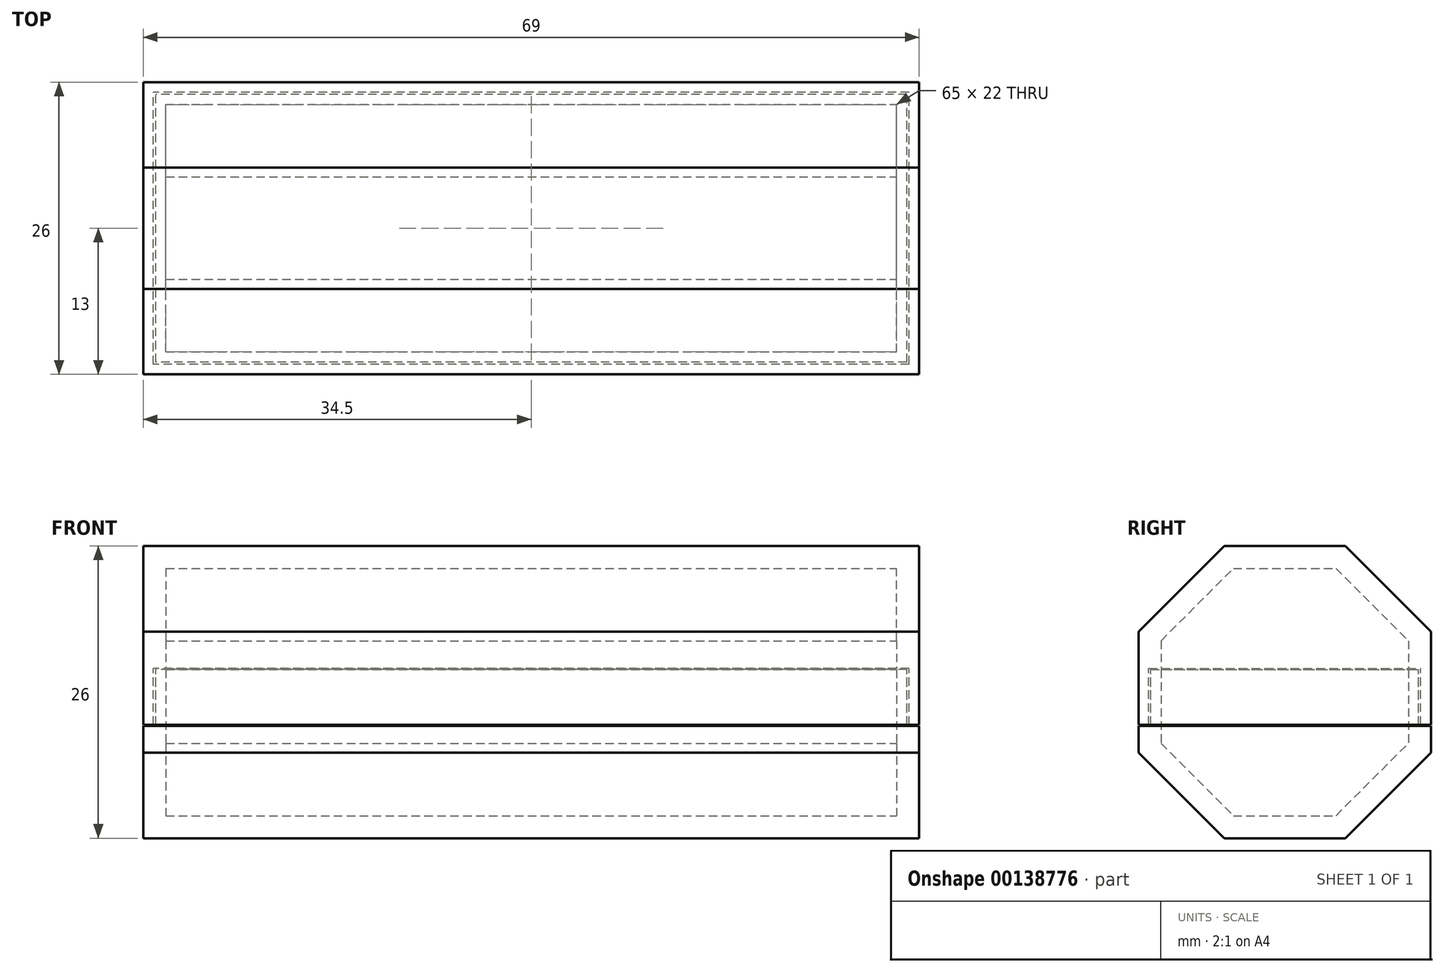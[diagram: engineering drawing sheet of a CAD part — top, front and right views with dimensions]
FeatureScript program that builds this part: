
annotation { "Feature Type Name" : "Feature", "Feature Type Description" : "" }
export const myFeature = defineFeature(function(context is Context, id is Id, definition is map)
    precondition{}
    {
        {
            var Q0;
            Q0=qCreatedBy(makeId("Top.planeOp"),FACE);
            var sketch = newSketch(context, id + "F0", { "sketchPlane" : qUnion([Q0])});
            skLineSegment(sketch, "E0.bottom", {"start": v(34.5, -13) * mm, "end": v(-34.5, -13) * mm});
            skLineSegment(sketch, "E0.top", {"start": v(34.5, 13) * mm, "end": v(-34.5, 13) * mm});
            skLineSegment(sketch, "E0.left", {"start": v(34.5, -13) * mm, "end": v(34.5, 13) * mm});
            skLineSegment(sketch, "E0.right", {"start": v(-34.5, -13) * mm, "end": v(-34.5, 13) * mm});
            skPoint(sketch, "E0.middle", {"position": v(0, 0) * mm});
            skSolve(sketch);
        }
        {
            var Q0;
            Q0 = qSketchRegion(id + "F0", true);
            extrude(context, id + "F1", {"entities" : qUnion([Q0]), "depth" : 15 * mm});
        }
        {
            var Q0;
            Q0=makeQuery(id+"F1.opExtrude","SWEPT_FACE",FACE,{"disambiguationData":[OSD([sQuery(id+"F0.wireOp",EDGE,"E0.left")])]});
            cPlane(context, id + "F2", {"entities" : qUnion([Q0]), "cplaneType" : CPlaneType.OFFSET, "offset" : 2 * mm, "oppositeDirection" : true, "width" : 150 * mm, "height" : 150 * mm});
        }
        {
            var Q0;
            Q0=qCreatedBy(id+"F2.planeOp",FACE);
            var sketch = newSketch(context, id + "F3", { "sketchPlane" : qUnion([Q0])});
            skLineSegment(sketch, "E1.0", {"start": v(13, 15) * mm, "end": v(13, 0) * mm, "construction": true});
            skLineSegment(sketch, "E2.0", {"start": v(-13, 0) * mm, "end": v(13, 0) * mm, "construction": true});
            skLineSegment(sketch, "E3.0", {"start": v(-13, 15) * mm, "end": v(-13, 0) * mm, "construction": true});
            skLineSegment(sketch, "E4.0", {"start": v(-13, 15) * mm, "end": v(13, 15) * mm, "construction": true});
            skLineSegment(sketch, "E5.1", {"start": v(-11, 15) * mm, "end": v(-11, 2) * mm, "construction": true});
            skLineSegment(sketch, "E5.2", {"start": v(-11, 2) * mm, "end": v(11, 2) * mm, "construction": true});
            skLineSegment(sketch, "E5.3", {"start": v(11, 15) * mm, "end": v(11, 2) * mm, "construction": true});
            skLineSegment(sketch, "E6", {"start": v(11, 8.5) * mm, "end": v(13, 8.5) * mm, "construction": true});
            skLineSegment(sketch, "E7", {"start": v(0, 2) * mm, "end": v(0, 0) * mm, "construction": true});
            skLineSegment(sketch, "E8", {"start": v(-11, 15) * mm, "end": v(-11, 8.44) * mm});
            skLineSegment(sketch, "E9", {"start": v(-11, 8.44) * mm, "end": v(-4.56, 2) * mm});
            skLineSegment(sketch, "E10", {"start": v(-4.56, 2) * mm, "end": v(4.56, 2) * mm});
            skLineSegment(sketch, "E11", {"start": v(4.56, 2) * mm, "end": v(11, 8.44) * mm});
            skLineSegment(sketch, "E12", {"start": v(-11, 15) * mm, "end": v(11, 15) * mm});
            skLineSegment(sketch, "E13", {"start": v(11, 15) * mm, "end": v(11, 8.44) * mm});
            skSolve(sketch);
        }
        {
            var Q0;
            Q0 = qSketchRegion(id + "F3", true);
            extrude(context, id + "F4", {"entities" : qUnion([Q0]), "operationType" : NewBodyOperationType.REMOVE, "oppositeDirection" : true, "depth" : 65 * mm});
        }
        {
            var Q0;
            Q0=makeQuery(id+"F1.opExtrude","CAP_FACE",FACE,{"disambiguationData":[OSD([sQuery(id+"F0.wireOp",EDGE,"E0.bottom"),sQuery(id+"F0.wireOp",EDGE,"E0.top"),sQuery(id+"F0.wireOp",EDGE,"E0.left"),sQuery(id+"F0.wireOp",EDGE,"E0.right")])],"isStart":false});
            var sketch = newSketch(context, id + "F5", { "sketchPlane" : qUnion([Q0])});
            skLineSegment(sketch, "E14.0", {"start": v(-33.4, -11.9) * mm, "end": v(-33.4, 11.9) * mm});
            skLineSegment(sketch, "E14.1", {"start": v(33.4, -11.9) * mm, "end": v(-33.4, -11.9) * mm});
            skLineSegment(sketch, "E14.2", {"start": v(33.4, -11.9) * mm, "end": v(33.4, 11.9) * mm});
            skLineSegment(sketch, "E14.3", {"start": v(33.4, 11.9) * mm, "end": v(-33.4, 11.9) * mm});
            skLineSegment(sketch, "E15.0", {"start": v(34.5, -13) * mm, "end": v(-34.5, -13) * mm});
            skLineSegment(sketch, "E16.0", {"start": v(34.5, 13) * mm, "end": v(-34.5, 13) * mm});
            skLineSegment(sketch, "E17.0", {"start": v(-34.5, -13) * mm, "end": v(-34.5, 13) * mm});
            skLineSegment(sketch, "E18.0", {"start": v(34.5, -13) * mm, "end": v(34.5, 13) * mm});
            skSolve(sketch);
        }
        {
            var Q0;
            Q0 = qSketchRegion(id + "F5", true);
            extrude(context, id + "F6", {"entities" : qUnion([Q0]), "operationType" : NewBodyOperationType.REMOVE, "oppositeDirection" : true, "depth" : 5 * mm});
        }
        {
            var Q0;
            Q0=makeQuery(id+"F1.opExtrude","CAP_FACE",FACE,{"disambiguationData":[OSD([sQuery(id+"F0.wireOp",EDGE,"E0.bottom"),sQuery(id+"F0.wireOp",EDGE,"E0.top"),sQuery(id+"F0.wireOp",EDGE,"E0.left"),sQuery(id+"F0.wireOp",EDGE,"E0.right")])],"isStart":false});
            cPlane(context, id + "F7", {"entities" : qUnion([Q0]), "cplaneType" : CPlaneType.OFFSET, "offset" : .1 * mm, "width" : 150 * mm, "height" : 150 * mm});
        }
        {
            var Q0;
            Q0=qCreatedBy(id+"F7.planeOp",FACE);
            var sketch = newSketch(context, id + "F8", { "sketchPlane" : qUnion([Q0])});
            skLineSegment(sketch, "E19.0", {"start": v(34.5, -13) * mm, "end": v(-34.5, -13) * mm});
            skLineSegment(sketch, "E20.0", {"start": v(-34.5, -13) * mm, "end": v(-34.5, 13) * mm});
            skLineSegment(sketch, "E21.0", {"start": v(34.5, 13) * mm, "end": v(-34.5, 13) * mm});
            skLineSegment(sketch, "E22.0", {"start": v(34.5, -13) * mm, "end": v(34.5, 13) * mm});
            skSolve(sketch);
        }
        {
            var Q0;
            Q0 = qSketchRegion(id + "F8", true);
            extrude(context, id + "F9", {"entities" : qUnion([Q0]), "depth" : 10.9 * mm});
        }
        {
            var Q0;
            Q0=makeQuery(id+"F9.opExtrude","CAP_FACE",FACE,{"disambiguationData":[OSD([sQuery(id+"F8.wireOp",EDGE,"E19.0"),sQuery(id+"F8.wireOp",EDGE,"E20.0"),sQuery(id+"F8.wireOp",EDGE,"E21.0"),sQuery(id+"F8.wireOp",EDGE,"E22.0")])],"isStart":true});
            var sketch = newSketch(context, id + "F10", { "sketchPlane" : qUnion([Q0])});
            skLineSegment(sketch, "E23.0", {"start": v(34.5, 13) * mm, "end": v(-34.5, 13) * mm});
            skLineSegment(sketch, "E24.0", {"start": v(34.5, 13) * mm, "end": v(34.5, -13) * mm});
            skLineSegment(sketch, "E25.0", {"start": v(34.5, -13) * mm, "end": v(-34.5, -13) * mm});
            skLineSegment(sketch, "E26.0", {"start": v(-34.5, 13) * mm, "end": v(-34.5, -13) * mm});
            skLineSegment(sketch, "E27.0", {"start": v(33.6, 12.1) * mm, "end": v(33.6, -12.1) * mm});
            skLineSegment(sketch, "E27.1", {"start": v(33.6, 12.1) * mm, "end": v(-33.6, 12.1) * mm});
            skLineSegment(sketch, "E27.2", {"start": v(-33.6, 12.1) * mm, "end": v(-33.6, -12.1) * mm});
            skLineSegment(sketch, "E27.3", {"start": v(33.6, -12.1) * mm, "end": v(-33.6, -12.1) * mm});
            skSolve(sketch);
        }
        {
            var Q0;
            Q0 = qSketchRegion(id + "F10", true);
            extrude(context, id + "F11", {"entities" : qUnion([Q0]), "operationType" : NewBodyOperationType.ADD, "depth" : 5 * mm});
        }
        {
            var Q0;
            Q0=qCreatedBy(id+"F2.planeOp",FACE);
            var sketch = newSketch(context, id + "F12", { "sketchPlane" : qUnion([Q0])});
            skLineSegment(sketch, "E28.0", {"start": v(-11, 8.44) * mm, "end": v(-4.56, 2) * mm, "construction": true});
            skLineSegment(sketch, "E29.0", {"start": v(4.56, 2) * mm, "end": v(11, 8.44) * mm, "construction": true});
            skLineSegment(sketch, "E30.0", {"start": v(-4.56, 2) * mm, "end": v(4.56, 2) * mm, "construction": true});
            skLineSegment(sketch, "E31.0", {"start": v(0, 2) * mm, "end": v(0, 0) * mm, "construction": true});
            skLineSegment(sketch, "E32.0", {"start": v(-13, 26) * mm, "end": v(13, 26) * mm, "construction": true});
            skLineSegment(sketch, "E33", {"start": v(0, 26) * mm, "end": v(0, 24) * mm, "construction": true});
            skPoint(sketch, "E33.endSnap0", {"position": v(0, 26) * mm});
            skLineSegment(sketch, "E34", {"start": v(-4.56, 24) * mm, "end": v(4.56, 24) * mm});
            skLineSegment(sketch, "E35", {"start": v(4.56, 24) * mm, "end": v(11, 17.56) * mm});
            skLineSegment(sketch, "E36.0", {"start": v(-12.1, 15.1) * mm, "end": v(12.1, 15.1) * mm, "construction": true});
            skLineSegment(sketch, "E37", {"start": v(-11, 17.56) * mm, "end": v(-4.56, 24) * mm});
            skLineSegment(sketch, "E38", {"start": v(-11, 8.44) * mm, "end": v(11, 8.44) * mm});
            skLineSegment(sketch, "E39", {"start": v(-11, 17.56) * mm, "end": v(-11, 8.44) * mm});
            skLineSegment(sketch, "E40", {"start": v(11, 17.56) * mm, "end": v(11, 8.44) * mm});
            skSolve(sketch);
        }
        {
            var Q0;
            Q0 = qSketchRegion(id + "F12", true);
            extrude(context, id + "F13", {"entities" : qUnion([Q0]), "operationType" : NewBodyOperationType.REMOVE, "oppositeDirection" : true, "depth" : 65 * mm});
        }
        {
            var Q0;
            Q0=makeQuery(id+"F1.opExtrude","SWEPT_FACE",FACE,{"disambiguationData":[OSD([sQuery(id+"F0.wireOp",EDGE,"E0.left")])]});
            var sketch = newSketch(context, id + "F14", { "sketchPlane" : qUnion([Q0])});
            skPoint(sketch, "E41.0", {"position": v(13, 0) * mm});
            skLineSegment(sketch, "E42.0", {"start": v(4.56, 2) * mm, "end": v(11, 8.44) * mm, "construction": true});
            skLineSegment(sketch, "E43", {"start": v(7.78, 5.22) * mm, "end": v(9.2, 3.8) * mm, "construction": true});
            skLineSegment(sketch, "E44", {"start": v(13, 0) * mm, "end": v(13, 7.62) * mm});
            skLineSegment(sketch, "E45", {"start": v(13, 7.62) * mm, "end": v(5.38, 0) * mm});
            skLineSegment(sketch, "E46", {"start": v(5.38, 0) * mm, "end": v(13, 0) * mm});
            skLineSegment(sketch, "E47.0", {"start": v(0, 2) * mm, "end": v(0, 0) * mm, "construction": true});
            skLineSegment(sketch, "E48.MirrorCS", {"start": v(-13, 7.62) * mm, "end": v(-5.38, 0) * mm});
            skLineSegment(sketch, "E49.MirrorCS", {"start": v(-13, 0) * mm, "end": v(-13, 7.62) * mm});
            skLineSegment(sketch, "E50.MirrorCS", {"start": v(-5.38, 0) * mm, "end": v(-13, 0) * mm});
            skSolve(sketch);
        }
        {
            var Q0;
            Q0 = qSketchRegion(id + "F14", true);
            extrude(context, id + "F15", {"entities" : qUnion([Q0]), "operationType" : NewBodyOperationType.REMOVE, "endBound" : BoundingType.THROUGH_ALL, "oppositeDirection" : true, "depth" : 25 * mm});
        }
        {
            var Q0;
            Q0=makeQuery(id+"F11.boolean.opBoolean","MERGE",FACE,{"derivedFrom":[makeQuery(id+"F9.opExtrude","SWEPT_FACE",FACE,{"disambiguationData":[OSD([sQuery(id+"F8.wireOp",EDGE,"E22.0")])]}),makeQuery(id+"F11.opExtrude","SWEPT_FACE",FACE,{"disambiguationData":[OSD([sQuery(id+"F10.wireOp",EDGE,"E24.0")])]})]});
            var sketch = newSketch(context, id + "F16", { "sketchPlane" : qUnion([Q0])});
            skLineSegment(sketch, "E51.0", {"start": v(-11, 17.56) * mm, "end": v(-4.56, 24) * mm, "construction": true});
            skPoint(sketch, "E52.0", {"position": v(-13, 26) * mm});
            skLineSegment(sketch, "E53.0", {"start": v(0, 26) * mm, "end": v(0, 24) * mm, "construction": true});
            skLineSegment(sketch, "E54", {"start": v(-7.78, 20.78) * mm, "end": v(-9.2, 22.2) * mm, "construction": true});
            skLineSegment(sketch, "E55", {"start": v(-13, 18.38) * mm, "end": v(-5.38, 26) * mm});
            skLineSegment(sketch, "E56", {"start": v(-5.38, 26) * mm, "end": v(-13, 26) * mm});
            skLineSegment(sketch, "E57", {"start": v(-13, 18.38) * mm, "end": v(-13, 26) * mm});
            skLineSegment(sketch, "E58.MirrorCS", {"start": v(13, 18.38) * mm, "end": v(5.38, 26) * mm});
            skLineSegment(sketch, "E59.MirrorCS", {"start": v(5.38, 26) * mm, "end": v(13, 26) * mm});
            skLineSegment(sketch, "E60.MirrorCS", {"start": v(13, 18.38) * mm, "end": v(13, 26) * mm});
            skSolve(sketch);
        }
        {
            var Q0;
            Q0 = qSketchRegion(id + "F16", true);
            extrude(context, id + "F17", {"entities" : qUnion([Q0]), "operationType" : NewBodyOperationType.REMOVE, "endBound" : BoundingType.THROUGH_ALL, "oppositeDirection" : true, "depth" : 25 * mm});
        }
    });
